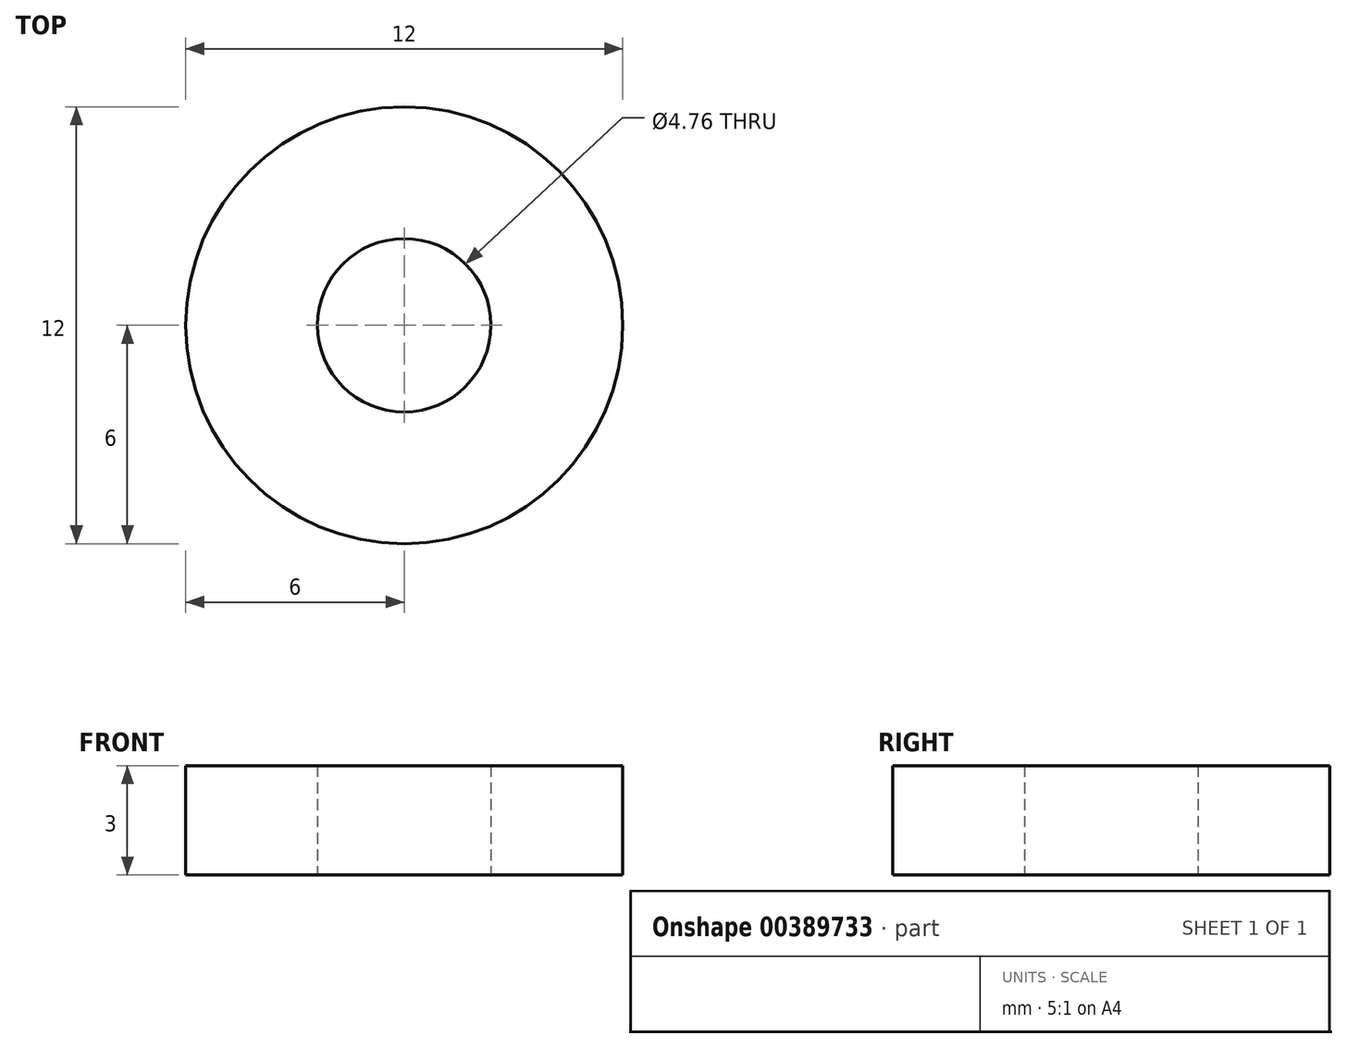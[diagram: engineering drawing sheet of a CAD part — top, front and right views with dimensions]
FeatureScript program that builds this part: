
annotation { "Feature Type Name" : "Feature", "Feature Type Description" : "" }
export const myFeature = defineFeature(function(context is Context, id is Id, definition is map)
    precondition{}
    {
        {
            var Q0;
            Q0=qCreatedBy(makeId("Top.planeOp"),FACE);
            var sketch = newSketch(context, id + "F0", { "sketchPlane" : qUnion([Q0])});
            skCircle(sketch, "E0", {"center": v(0, 0) * mm, "radius": 6 * mm});
            skCircle(sketch, "E1", {"center": v(0, 0) * mm, "radius": 2.38 * mm});
            skSolve(sketch);
        }
        {
            var Q0;
            Q0 = qSketchRegion(id + "F0", true);
            extrude(context, id + "F1", {"entities" : qUnion([Q0]), "depth" : 3 * mm});
        }
    });
